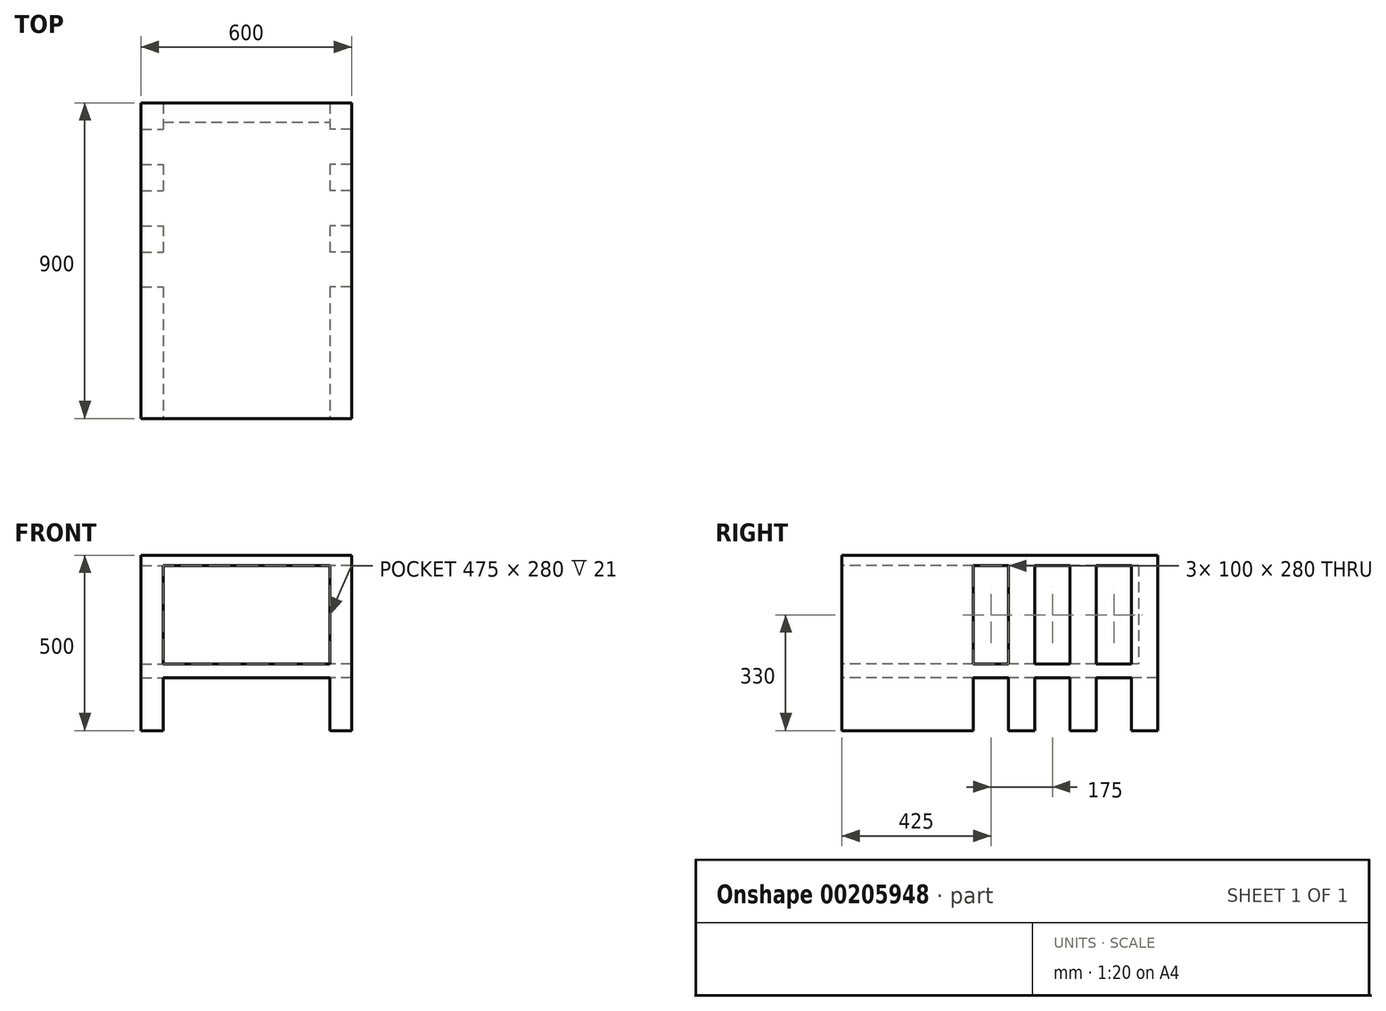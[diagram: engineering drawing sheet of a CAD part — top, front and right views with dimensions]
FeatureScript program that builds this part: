
annotation { "Feature Type Name" : "Feature", "Feature Type Description" : "" }
export const myFeature = defineFeature(function(context is Context, id is Id, definition is map)
    precondition{}
    {
        {
            var Q0;
            Q0=qCreatedBy(makeId("Top.planeOp"),FACE);
            var sketch = newSketch(context, id + "F0", { "sketchPlane" : qUnion([Q0])});
            skLineSegment(sketch, "E0.bottom", {"start": v(300, 450) * mm, "end": v(-300, 450) * mm});
            skLineSegment(sketch, "E0.top", {"start": v(300, -450) * mm, "end": v(-300, -450) * mm});
            skLineSegment(sketch, "E0.left", {"start": v(300, 450) * mm, "end": v(300, -450) * mm});
            skLineSegment(sketch, "E0.right", {"start": v(-300, 450) * mm, "end": v(-300, -450) * mm});
            skPoint(sketch, "E0.middle", {"position": v(0, 0) * mm});
            skSolve(sketch);
        }
        {
            var Q0;
            Q0=makeQuery(id+"F0.imprint","IMPRINT",FACE,{"disambiguationData":[TD([[makeQuery(id+"F0.imprint","IMPRINT",EDGE,{"derivedFrom":sQuery(id+"F0.wireOp",EDGE,"E0.bottom")}),1.0]])]});
            extrude(context, id + "F1", {"entities" : qUnion([Q0]), "depth" : 500 * mm});
        }
        {
            var Q0;
            Q0=makeQuery(id+"F1.opExtrude","SWEPT_FACE",FACE,{"disambiguationData":[OSD([sQuery(id+"F0.wireOp",EDGE,"E0.top")])]});
            var sketch = newSketch(context, id + "F2", { "sketchPlane" : qUnion([Q0])});
            skLineSegment(sketch, "E1.bottom", {"start": v(-237.5, 0) * mm, "end": v(237.5, 0) * mm});
            skLineSegment(sketch, "E1.top", {"start": v(-237.5, 150) * mm, "end": v(237.5, 150) * mm});
            skLineSegment(sketch, "E1.left", {"start": v(-237.5, 0) * mm, "end": v(-237.5, 150) * mm});
            skLineSegment(sketch, "E1.right", {"start": v(237.5, 0) * mm, "end": v(237.5, 150) * mm});
            skSolve(sketch);
        }
        {
            var Q0;
            Q0=makeQuery(id+"F2.imprint","IMPRINT",FACE,{"disambiguationData":[TD([[makeQuery(id+"F2.imprint","IMPRINT",EDGE,{"derivedFrom":sQuery(id+"F2.wireOp",EDGE,"E1.bottom")}),-1.0]])]});
            extrude(context, id + "F3", {"entities" : qUnion([Q0]), "operationType" : NewBodyOperationType.REMOVE, "oppositeDirection" : true, "depth" : 1705 * mm});
        }
        {
            var Q0;
            Q0=makeQuery(id+"F1.opExtrude","SWEPT_FACE",FACE,{"disambiguationData":[OSD([sQuery(id+"F0.wireOp",EDGE,"E0.top")])]});
            var sketch = newSketch(context, id + "F4", { "sketchPlane" : qUnion([Q0])});
            skLineSegment(sketch, "E2.bottom", {"start": v(-237.5, 470) * mm, "end": v(237.5, 470) * mm});
            skLineSegment(sketch, "E2.top", {"start": v(-237.5, 190) * mm, "end": v(237.5, 190) * mm});
            skLineSegment(sketch, "E2.left", {"start": v(-237.5, 470) * mm, "end": v(-237.5, 190) * mm});
            skLineSegment(sketch, "E2.right", {"start": v(237.5, 470) * mm, "end": v(237.5, 190) * mm});
            skSolve(sketch);
        }
        {
            var Q0;
            Q0=makeQuery(id+"F4.imprint","IMPRINT",FACE,{"disambiguationData":[TD([[makeQuery(id+"F4.imprint","IMPRINT",EDGE,{"derivedFrom":sQuery(id+"F4.wireOp",EDGE,"E2.bottom")}),-1.0]])]});
            extrude(context, id + "F5", {"entities" : qUnion([Q0]), "operationType" : NewBodyOperationType.REMOVE, "oppositeDirection" : true, "depth" : 846 * mm});
        }
        {
            var Q0;
            Q0=makeQuery(id+"F1.opExtrude","SWEPT_FACE",FACE,{"disambiguationData":[OSD([sQuery(id+"F0.wireOp",EDGE,"E0.left")])]});
            var sketch = newSketch(context, id + "F6", { "sketchPlane" : qUnion([Q0])});
            skLineSegment(sketch, "E3.bottom", {"start": v(375, 500) * mm, "end": v(275, 500) * mm});
            skLineSegment(sketch, "E3.top", {"start": v(375, 0) * mm, "end": v(275, 0) * mm});
            skLineSegment(sketch, "E3.left", {"start": v(375, 500) * mm, "end": v(375, 0) * mm});
            skLineSegment(sketch, "E3.right", {"start": v(275, 500) * mm, "end": v(275, 0) * mm});
            skLineSegment(sketch, "E4.bottom", {"start": v(200, 500) * mm, "end": v(100, 500) * mm});
            skLineSegment(sketch, "E4.top", {"start": v(200, 0) * mm, "end": v(100, 0) * mm});
            skLineSegment(sketch, "E4.left", {"start": v(200, 500) * mm, "end": v(200, 0) * mm});
            skLineSegment(sketch, "E4.right", {"start": v(100, 500) * mm, "end": v(100, 0) * mm});
            skLineSegment(sketch, "E5.bottom", {"start": v(-75, 500) * mm, "end": v(25, 500) * mm});
            skLineSegment(sketch, "E5.top", {"start": v(-75, 0) * mm, "end": v(25, 0) * mm});
            skLineSegment(sketch, "E5.left", {"start": v(-75, 500) * mm, "end": v(-75, 0) * mm});
            skLineSegment(sketch, "E5.right", {"start": v(25, 500) * mm, "end": v(25, 0) * mm});
            skSolve(sketch);
        }
        {
            var Q0;
            Q0=makeQuery(id+"F6.imprint","IMPRINT",FACE,{"disambiguationData":[TD([[makeQuery(id+"F6.imprint","IMPRINT",EDGE,{"derivedFrom":sQuery(id+"F6.wireOp",EDGE,"E5.bottom")}),1.0]])]});
            extrude(context, id + "F7", {"entities" : qUnion([Q0]), "operationType" : NewBodyOperationType.REMOVE, "oppositeDirection" : true, "depth" : 63 * mm});
        }
        {
            var Q0;
            {var subQ0=sQuery(id+"F6.wireOp",EDGE,"E5.right");var subQ1=sQuery(id+"F6.wireOp",EDGE,"E5.left");Q0=makeQuery(id+"F7.boolean.opBoolean","COPY",FACE,{"disambiguationData":[TD([makeQuery(id+"F5.boolean.opBoolean","COPY",FACE,{"derivedFrom":makeQuery(id+"F5.opExtrude","SWEPT_FACE",FACE,{"disambiguationData":[OSD([sQuery(id+"F4.wireOp",EDGE,"E2.bottom")])]})})])],"derivedFrom":makeQuery(id+"F7.opExtrude","CAP_FACE",FACE,{"disambiguationData":[OSD([sQuery(id+"F6.wireOp",EDGE,"E5.bottom"),sQuery(id+"F6.wireOp",EDGE,"E5.top"),subQ1,subQ0])],"isStart":false})});}
            extrude(context, id + "F8", {"entities" : qUnion([Q0]), "operationType" : NewBodyOperationType.ADD, "depth" : 63 * mm});
        }
        {
            var Q0;
            {var subQ0=sQuery(id+"F6.wireOp",EDGE,"E5.left");var subQ1=sQuery(id+"F6.wireOp",EDGE,"E5.right");Q0=makeQuery(id+"F7.boolean.opBoolean","COPY",FACE,{"disambiguationData":[TD([makeQuery(id+"F3.boolean.opBoolean","COPY",FACE,{"derivedFrom":makeQuery(id+"F3.opExtrude","SWEPT_FACE",FACE,{"disambiguationData":[OSD([sQuery(id+"F2.wireOp",EDGE,"E1.top")])]})})])],"derivedFrom":makeQuery(id+"F7.opExtrude","CAP_FACE",FACE,{"disambiguationData":[OSD([sQuery(id+"F6.wireOp",EDGE,"E5.bottom"),sQuery(id+"F6.wireOp",EDGE,"E5.top"),subQ0,subQ1])],"isStart":false})});}
            extrude(context, id + "F9", {"entities" : qUnion([Q0]), "operationType" : NewBodyOperationType.ADD, "depth" : 63 * mm});
        }
        {
            var Q0;
            Q0 = qSketchRegion(id + "F6", true);
            extrude(context, id + "F10", {"entities" : qUnion([Q0]), "operationType" : NewBodyOperationType.REMOVE, "oppositeDirection" : true, "depth" : 63 * mm});
        }
        {
            var Q0;
            {var subQ0=sQuery(id+"F4.wireOp",EDGE,"E2.bottom");var subQ1=sQuery(id+"F6.wireOp",EDGE,"E5.right");var subQ2=sQuery(id+"F6.wireOp",EDGE,"E5.left");var subQ3=sQuery(id+"F6.wireOp",EDGE,"E5.bottom");var subQ4=sQuery(id+"F6.wireOp",EDGE,"E5.top");Q0=makeQuery(id+"F10.boolean.opBoolean","COPY",FACE,{"disambiguationData":[TD([makeQuery(id+"F5.boolean.opBoolean","COPY",FACE,{"derivedFrom":makeQuery(id+"F5.opExtrude","SWEPT_FACE",FACE,{"disambiguationData":[OSD([subQ0])]})})])],"derivedFrom":makeQuery(id+"F10.opExtrude","CAP_FACE",FACE,{"disambiguationData":[OSD([subQ3,subQ4,subQ2,subQ1])],"isStart":false})});}
            var Q1;
            {var subQ1=sQuery(id+"F4.wireOp",EDGE,"E2.bottom");var subQ2=sQuery(id+"F6.wireOp",EDGE,"E4.right");var subQ3=sQuery(id+"F6.wireOp",EDGE,"E4.left");Q1=makeQuery(id+"F10.boolean.opBoolean","COPY",FACE,{"disambiguationData":[TD([makeQuery(id+"F5.boolean.opBoolean","COPY",FACE,{"derivedFrom":makeQuery(id+"F5.opExtrude","SWEPT_FACE",FACE,{"disambiguationData":[OSD([subQ1])]})})])],"derivedFrom":makeQuery(id+"F10.opExtrude","CAP_FACE",FACE,{"disambiguationData":[OSD([sQuery(id+"F6.wireOp",EDGE,"E4.bottom"),sQuery(id+"F6.wireOp",EDGE,"E4.top"),subQ3,subQ2])],"isStart":false})});}
            var Q2;
            {var subQ1=sQuery(id+"F6.wireOp",EDGE,"E3.left");var subQ2=sQuery(id+"F4.wireOp",EDGE,"E2.bottom");var subQ3=sQuery(id+"F6.wireOp",EDGE,"E3.right");Q2=makeQuery(id+"F10.boolean.opBoolean","COPY",FACE,{"disambiguationData":[TD([makeQuery(id+"F5.boolean.opBoolean","COPY",FACE,{"derivedFrom":makeQuery(id+"F5.opExtrude","SWEPT_FACE",FACE,{"disambiguationData":[OSD([subQ2])]})})])],"derivedFrom":makeQuery(id+"F10.opExtrude","CAP_FACE",FACE,{"disambiguationData":[OSD([sQuery(id+"F6.wireOp",EDGE,"E3.bottom"),sQuery(id+"F6.wireOp",EDGE,"E3.top"),subQ1,subQ3])],"isStart":false})});}
            var Q3;
            {var subQ5=sQuery(id+"F6.wireOp",EDGE,"E3.right");var subQ6=sQuery(id+"F2.wireOp",EDGE,"E1.top");var subQ7=sQuery(id+"F6.wireOp",EDGE,"E3.left");Q3=makeQuery(id+"F10.boolean.opBoolean","COPY",FACE,{"disambiguationData":[TD([makeQuery(id+"F3.boolean.opBoolean","COPY",FACE,{"derivedFrom":makeQuery(id+"F3.opExtrude","SWEPT_FACE",FACE,{"disambiguationData":[OSD([subQ6])]})})])],"derivedFrom":makeQuery(id+"F10.opExtrude","CAP_FACE",FACE,{"disambiguationData":[OSD([sQuery(id+"F6.wireOp",EDGE,"E3.bottom"),sQuery(id+"F6.wireOp",EDGE,"E3.top"),subQ7,subQ5])],"isStart":false})});}
            var Q4;
            {var subQ5=sQuery(id+"F2.wireOp",EDGE,"E1.top");var subQ6=sQuery(id+"F6.wireOp",EDGE,"E4.left");var subQ7=sQuery(id+"F6.wireOp",EDGE,"E4.right");Q4=makeQuery(id+"F10.boolean.opBoolean","COPY",FACE,{"disambiguationData":[TD([makeQuery(id+"F3.boolean.opBoolean","COPY",FACE,{"derivedFrom":makeQuery(id+"F3.opExtrude","SWEPT_FACE",FACE,{"disambiguationData":[OSD([subQ5])]})})])],"derivedFrom":makeQuery(id+"F10.opExtrude","CAP_FACE",FACE,{"disambiguationData":[OSD([sQuery(id+"F6.wireOp",EDGE,"E4.bottom"),sQuery(id+"F6.wireOp",EDGE,"E4.top"),subQ6,subQ7])],"isStart":false})});}
            var Q5;
            {var subQ0=sQuery(id+"F6.wireOp",EDGE,"E5.right");var subQ2=sQuery(id+"F6.wireOp",EDGE,"E5.left");var subQ3=sQuery(id+"F2.wireOp",EDGE,"E1.top");var subQ4=sQuery(id+"F6.wireOp",EDGE,"E5.top");var subQ5=sQuery(id+"F6.wireOp",EDGE,"E5.bottom");Q5=makeQuery(id+"F10.boolean.opBoolean","COPY",FACE,{"disambiguationData":[TD([makeQuery(id+"F3.boolean.opBoolean","COPY",FACE,{"derivedFrom":makeQuery(id+"F3.opExtrude","SWEPT_FACE",FACE,{"disambiguationData":[OSD([subQ3])]})})])],"derivedFrom":makeQuery(id+"F10.opExtrude","CAP_FACE",FACE,{"disambiguationData":[OSD([subQ5,subQ4,subQ2,subQ0])],"isStart":false})});}
            extrude(context, id + "F11", {"entities" : qUnion([Q0, Q1, Q2, Q3, Q4, Q5]), "operationType" : NewBodyOperationType.ADD, "depth" : 63 * mm});
        }
        {
            var Q0;
            Q0=makeQuery(id+"F1.opExtrude","SWEPT_FACE",FACE,{"disambiguationData":[OSD([sQuery(id+"F0.wireOp",EDGE,"E0.right")])]});
            var sketch = newSketch(context, id + "F12", { "sketchPlane" : qUnion([Q0])});
            skSolve(sketch);
        }
        {
            var Q0;
            {var subQ0=sQuery(id+"F0.wireOp",EDGE,"E0.right");Q0=makeQuery(id+"F12.imprint","IMPRINT",FACE,{"disambiguationData":[TD([[makeQuery(id+"F12.imprint","IMPRINT",EDGE,{"derivedFrom":makeQuery(id+"F1.opExtrude","CAP_EDGE",EDGE,{"disambiguationData":[OSD([subQ0])],"isStart":true})}),1.0]])]});}
            var sketch = newSketch(context, id + "F13", { "sketchPlane" : qUnion([Q0])});
            skLineSegment(sketch, "E6.bottom", {"start": v(-375, 500) * mm, "end": v(-275, 500) * mm});
            skLineSegment(sketch, "E6.top", {"start": v(-375, 0) * mm, "end": v(-275, 0) * mm});
            skLineSegment(sketch, "E6.left", {"start": v(-375, 500) * mm, "end": v(-375, 0) * mm});
            skLineSegment(sketch, "E6.right", {"start": v(-275, 500) * mm, "end": v(-275, 0) * mm});
            skPoint(sketch, "E7.firstSnap0", {"position": v(-325, 500) * mm});
            skLineSegment(sketch, "E7.bottom", {"start": v(-200, 500) * mm, "end": v(-100, 500) * mm});
            skLineSegment(sketch, "E7.top", {"start": v(-200, 0) * mm, "end": v(-100, 0) * mm});
            skLineSegment(sketch, "E7.left", {"start": v(-200, 500) * mm, "end": v(-200, 0) * mm});
            skLineSegment(sketch, "E7.right", {"start": v(-100, 500) * mm, "end": v(-100, 0) * mm});
            skLineSegment(sketch, "E8.bottom", {"start": v(-25, 500) * mm, "end": v(75, 500) * mm});
            skLineSegment(sketch, "E8.top", {"start": v(-25, 0) * mm, "end": v(75, 0) * mm});
            skLineSegment(sketch, "E8.left", {"start": v(-25, 500) * mm, "end": v(-25, 0) * mm});
            skLineSegment(sketch, "E8.right", {"start": v(75, 500) * mm, "end": v(75, 0) * mm});
            skSolve(sketch);
        }
        {
            var Q0;
            Q0=makeQuery(id+"F13.imprint","IMPRINT",FACE,{"disambiguationData":[TD([[makeQuery(id+"F13.imprint","IMPRINT",EDGE,{"derivedFrom":sQuery(id+"F13.wireOp",EDGE,"E6.bottom")}),-1.0]])]});
            var Q1;
            Q1=makeQuery(id+"F13.imprint","IMPRINT",FACE,{"disambiguationData":[TD([[makeQuery(id+"F13.imprint","IMPRINT",EDGE,{"derivedFrom":sQuery(id+"F13.wireOp",EDGE,"E7.bottom")}),-1.0]])]});
            var Q2;
            Q2=makeQuery(id+"F13.imprint","IMPRINT",FACE,{"disambiguationData":[TD([[makeQuery(id+"F13.imprint","IMPRINT",EDGE,{"derivedFrom":sQuery(id+"F13.wireOp",EDGE,"E8.bottom")}),-1.0]])]});
            extrude(context, id + "F14", {"entities" : qUnion([Q0, Q1, Q2]), "operationType" : NewBodyOperationType.REMOVE, "oppositeDirection" : true, "depth" : 63 * mm});
        }
        {
            var Q0;
            {var subQ5=sQuery(id+"F4.wireOp",EDGE,"E2.bottom");var subQ7=sQuery(id+"F13.wireOp",EDGE,"E6.right");var subQ8=sQuery(id+"F13.wireOp",EDGE,"E6.left");Q0=makeQuery(id+"F14.boolean.opBoolean","COPY",FACE,{"disambiguationData":[TD([makeQuery(id+"F5.boolean.opBoolean","COPY",FACE,{"derivedFrom":makeQuery(id+"F5.opExtrude","SWEPT_FACE",FACE,{"disambiguationData":[OSD([subQ5])]})})])],"derivedFrom":makeQuery(id+"F14.opExtrude","CAP_FACE",FACE,{"disambiguationData":[OSD([sQuery(id+"F13.wireOp",EDGE,"E6.bottom"),sQuery(id+"F13.wireOp",EDGE,"E6.top"),subQ8,subQ7])],"isStart":false})});}
            var Q1;
            {var subQ5=sQuery(id+"F4.wireOp",EDGE,"E2.bottom");var subQ7=sQuery(id+"F13.wireOp",EDGE,"E7.left");var subQ8=sQuery(id+"F13.wireOp",EDGE,"E7.right");Q1=makeQuery(id+"F14.boolean.opBoolean","COPY",FACE,{"disambiguationData":[TD([makeQuery(id+"F5.boolean.opBoolean","COPY",FACE,{"derivedFrom":makeQuery(id+"F5.opExtrude","SWEPT_FACE",FACE,{"disambiguationData":[OSD([subQ5])]})})])],"derivedFrom":makeQuery(id+"F14.opExtrude","CAP_FACE",FACE,{"disambiguationData":[OSD([sQuery(id+"F13.wireOp",EDGE,"E7.bottom"),sQuery(id+"F13.wireOp",EDGE,"E7.top"),subQ7,subQ8])],"isStart":false})});}
            var Q2;
            {var subQ5=sQuery(id+"F4.wireOp",EDGE,"E2.bottom");var subQ7=sQuery(id+"F13.wireOp",EDGE,"E8.right");var subQ8=sQuery(id+"F13.wireOp",EDGE,"E8.left");Q2=makeQuery(id+"F14.boolean.opBoolean","COPY",FACE,{"disambiguationData":[TD([makeQuery(id+"F5.boolean.opBoolean","COPY",FACE,{"derivedFrom":makeQuery(id+"F5.opExtrude","SWEPT_FACE",FACE,{"disambiguationData":[OSD([subQ5])]})})])],"derivedFrom":makeQuery(id+"F14.opExtrude","CAP_FACE",FACE,{"disambiguationData":[OSD([sQuery(id+"F13.wireOp",EDGE,"E8.bottom"),sQuery(id+"F13.wireOp",EDGE,"E8.top"),subQ8,subQ7])],"isStart":false})});}
            extrude(context, id + "F15", {"entities" : qUnion([Q0, Q1, Q2]), "operationType" : NewBodyOperationType.ADD, "depth" : 63 * mm});
        }
        {
            var Q0;
            {var subQ13=sQuery(id+"F2.wireOp",EDGE,"E1.top");var subQ14=sQuery(id+"F13.wireOp",EDGE,"E6.left");var subQ15=sQuery(id+"F13.wireOp",EDGE,"E6.right");Q0=makeQuery(id+"F14.boolean.opBoolean","COPY",FACE,{"disambiguationData":[TD([makeQuery(id+"F3.boolean.opBoolean","COPY",FACE,{"derivedFrom":makeQuery(id+"F3.opExtrude","SWEPT_FACE",FACE,{"disambiguationData":[OSD([subQ13])]})})])],"derivedFrom":makeQuery(id+"F14.opExtrude","CAP_FACE",FACE,{"disambiguationData":[OSD([sQuery(id+"F13.wireOp",EDGE,"E6.bottom"),sQuery(id+"F13.wireOp",EDGE,"E6.top"),subQ14,subQ15])],"isStart":false})});}
            var Q1;
            {var subQ13=sQuery(id+"F2.wireOp",EDGE,"E1.top");var subQ14=sQuery(id+"F13.wireOp",EDGE,"E7.left");var subQ15=sQuery(id+"F13.wireOp",EDGE,"E7.right");Q1=makeQuery(id+"F14.boolean.opBoolean","COPY",FACE,{"disambiguationData":[TD([makeQuery(id+"F3.boolean.opBoolean","COPY",FACE,{"derivedFrom":makeQuery(id+"F3.opExtrude","SWEPT_FACE",FACE,{"disambiguationData":[OSD([subQ13])]})})])],"derivedFrom":makeQuery(id+"F14.opExtrude","CAP_FACE",FACE,{"disambiguationData":[OSD([sQuery(id+"F13.wireOp",EDGE,"E7.bottom"),sQuery(id+"F13.wireOp",EDGE,"E7.top"),subQ14,subQ15])],"isStart":false})});}
            var Q2;
            {var subQ13=sQuery(id+"F2.wireOp",EDGE,"E1.top");var subQ14=sQuery(id+"F13.wireOp",EDGE,"E8.left");var subQ15=sQuery(id+"F13.wireOp",EDGE,"E8.right");Q2=makeQuery(id+"F14.boolean.opBoolean","COPY",FACE,{"disambiguationData":[TD([makeQuery(id+"F3.boolean.opBoolean","COPY",FACE,{"derivedFrom":makeQuery(id+"F3.opExtrude","SWEPT_FACE",FACE,{"disambiguationData":[OSD([subQ13])]})})])],"derivedFrom":makeQuery(id+"F14.opExtrude","CAP_FACE",FACE,{"disambiguationData":[OSD([sQuery(id+"F13.wireOp",EDGE,"E8.bottom"),sQuery(id+"F13.wireOp",EDGE,"E8.top"),subQ14,subQ15])],"isStart":false})});}
            extrude(context, id + "F16", {"entities" : qUnion([Q0, Q1, Q2]), "operationType" : NewBodyOperationType.ADD, "depth" : 63 * mm});
        }
    });
